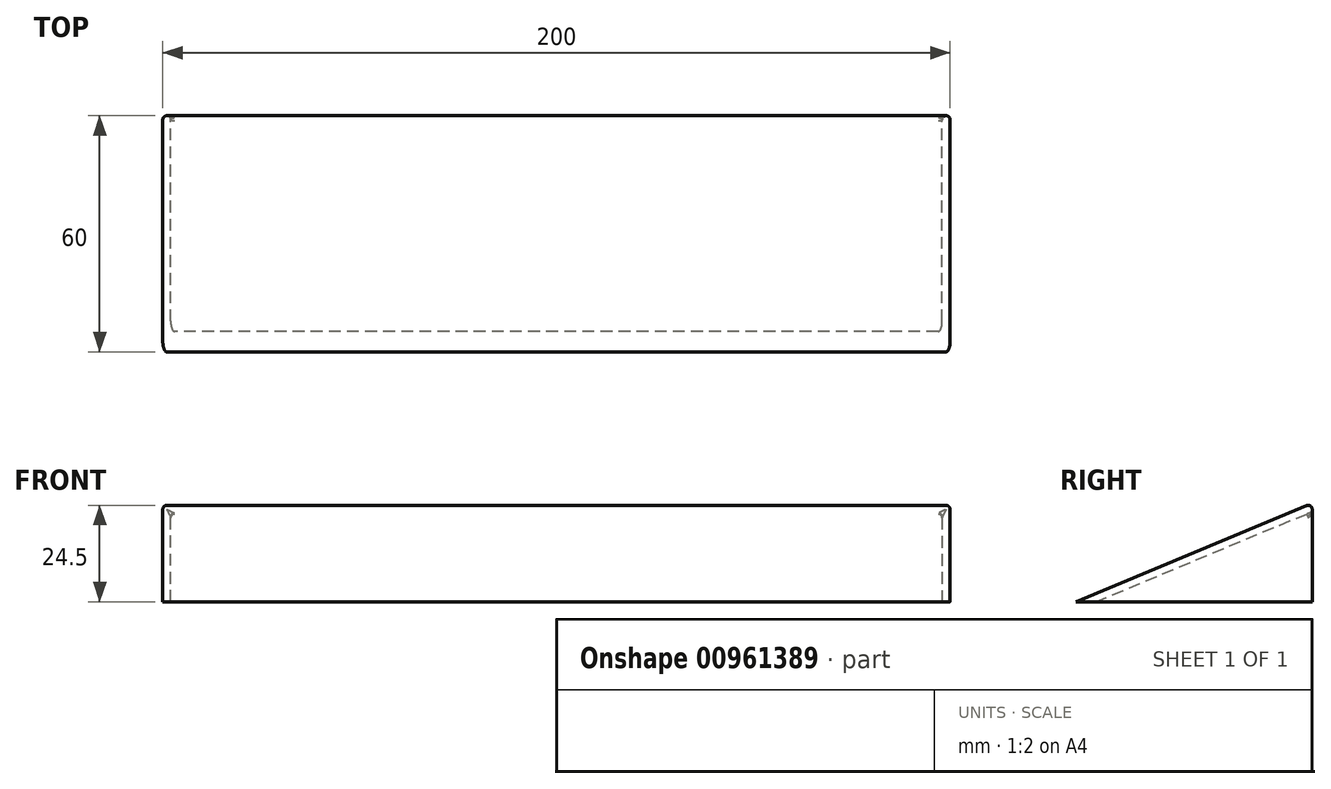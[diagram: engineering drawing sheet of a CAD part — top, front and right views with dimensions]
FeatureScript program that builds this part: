
annotation { "Feature Type Name" : "Feature", "Feature Type Description" : "" }
export const myFeature = defineFeature(function(context is Context, id is Id, definition is map)
    precondition{}
    {
        {
            var Q0;
            Q0=qCreatedBy(makeId("Right.planeOp"),FACE);
            var sketch = newSketch(context, id + "F0", { "sketchPlane" : qUnion([Q0])});
            skLineSegment(sketch, "E0", {"start": v(0, 0) * mm, "end": v(60, 0) * mm});
            skLineSegment(sketch, "E1", {"start": v(60, 0) * mm, "end": v(60, 25) * mm});
            skLineSegment(sketch, "E2", {"start": v(60, 25) * mm, "end": v(0, 0) * mm});
            skSolve(sketch);
        }
        {
            var Q0;
            Q0=makeQuery(id+"F0.imprint","IMPRINT",FACE,{"disambiguationData":[TD([[makeQuery(id+"F0.imprint","IMPRINT",EDGE,{"derivedFrom":sQuery(id+"F0.wireOp",EDGE,"E0")}),1.0]])]});
            extrude(context, id + "F1", {"entities" : qUnion([Q0]), "endBound" : BoundingType.SYMMETRIC, "depth" : 200 * mm, "offsetDistance" : 25 * mm});
        }
        {
            var Q0;
            Q0=makeQuery(id+"F1.opExtrude","SWEPT_FACE",FACE,{"disambiguationData":[OSD([sQuery(id+"F0.wireOp",EDGE,"E1")])]});
            var Q1;
            Q1=makeQuery(id+"F1.opExtrude","SWEPT_FACE",FACE,{"disambiguationData":[OSD([sQuery(id+"F0.wireOp",EDGE,"E0")])]});
            shell(context, id + "F2", {"entities" : qUnion([Q0, Q1]), "thickness" : 2 * mm});
        }
        {
            var Q0;
            Q0=makeQuery(id+"F1.opExtrude","CAP_EDGE",EDGE,{"disambiguationData":[OSD([sQuery(id+"F0.wireOp",EDGE,"E1")])],"isStart":false});
            var Q1;
            {var subQ0=sQuery(id+"F0.wireOp",EDGE,"E1");Q1=makeQuery(id+"F2.opShell","OFFSET_EDGE",EDGE,{"disambiguationData":[OSD([subQ0]),TDD([makeQuery(id+"F1.opExtrude","CAP_EDGE",EDGE,{"disambiguationData":[OSD([subQ0])],"isStart":false})])]});}
            var Q2;
            Q2=makeQuery(id+"F1.opExtrude","CAP_EDGE",EDGE,{"disambiguationData":[OSD([sQuery(id+"F0.wireOp",EDGE,"E1")])],"isStart":true});
            var Q3;
            {var subQ0=sQuery(id+"F0.wireOp",EDGE,"E1");Q3=makeQuery(id+"F2.opShell","OFFSET_EDGE",EDGE,{"disambiguationData":[OSD([subQ0]),TDD([makeQuery(id+"F1.opExtrude","CAP_EDGE",EDGE,{"disambiguationData":[OSD([subQ0])],"isStart":true})])]});}
            var Q4;
            Q4=makeQuery(id+"F2.opShell","OFFSET_EDGE",EDGE,{"disambiguationData":[OSD([sQuery(id+"F0.wireOp",EDGE,"E1"),sQuery(id+"F0.wireOp",EDGE,"E2")])]});
            var Q5;
            Q5=makeQuery(id+"F1.opExtrude","SWEPT_EDGE",EDGE,{"disambiguationData":[OSD([sQuery(id+"F0.wireOp",EDGE,"E1"),sQuery(id+"F0.wireOp",EDGE,"E2")])]});
            var Q6;
            Q6=makeQuery(id+"F1.opExtrude","CAP_EDGE",EDGE,{"disambiguationData":[OSD([sQuery(id+"F0.wireOp",EDGE,"E2")])],"isStart":false});
            var Q7;
            Q7=makeQuery(id+"F1.opExtrude","CAP_EDGE",EDGE,{"disambiguationData":[OSD([sQuery(id+"F0.wireOp",EDGE,"E2")])],"isStart":true});
            fillet(context, id + "F3", {"entities" : qUnion([Q0, Q1, Q2, Q3, Q4, Q5, Q6, Q7]), "radius" : 1 * mm, "tangentPropagation" : true, "allowEdgeOverflow" : false});
        }
        {
            var Q0;
            {var subQ0=sQuery(id+"F0.wireOp",EDGE,"E2");Q0=makeQuery(id+"F2.opShell","OFFSET_EDGE",EDGE,{"disambiguationData":[OSD([subQ0]),TDD([makeQuery(id+"F1.opExtrude","CAP_EDGE",EDGE,{"disambiguationData":[OSD([subQ0])],"isStart":false})])]});}
            var Q1;
            {var subQ0=sQuery(id+"F0.wireOp",EDGE,"E2");Q1=makeQuery(id+"F2.opShell","OFFSET_EDGE",EDGE,{"disambiguationData":[OSD([subQ0]),TDD([makeQuery(id+"F1.opExtrude","CAP_EDGE",EDGE,{"disambiguationData":[OSD([subQ0])],"isStart":true})])]});}
            fillet(context, id + "F4", {"entities" : qUnion([Q0, Q1]), "radius" : 1 * mm, "tangentPropagation" : true, "allowEdgeOverflow" : false});
        }
    });
